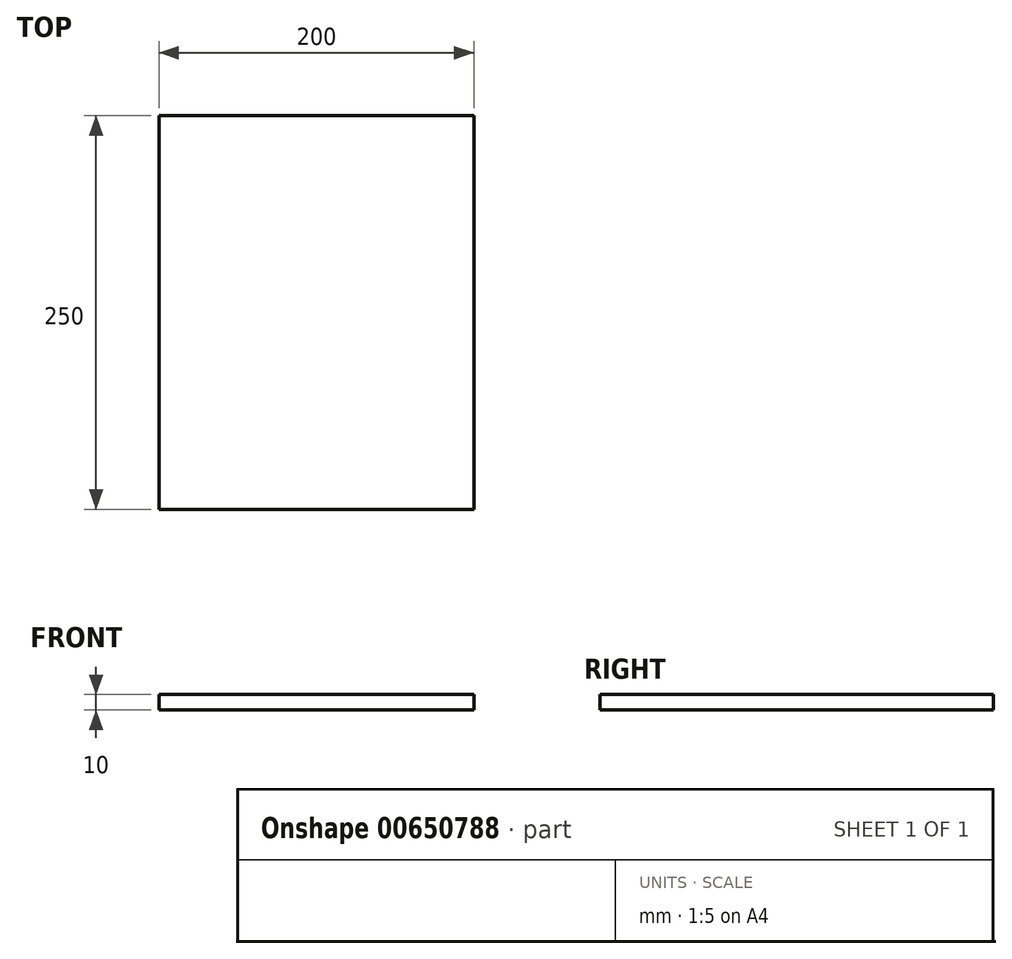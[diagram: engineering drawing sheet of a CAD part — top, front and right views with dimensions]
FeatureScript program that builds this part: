
annotation { "Feature Type Name" : "Feature", "Feature Type Description" : "" }
export const myFeature = defineFeature(function(context is Context, id is Id, definition is map)
    precondition{}
    {
        {
            var Q0;
            Q0=qCreatedBy(makeId("Top.planeOp"),FACE);
            var sketch = newSketch(context, id + "F0", { "sketchPlane" : qUnion([Q0])});
            skLineSegment(sketch, "E0.bottom", {"start": v(-157.02, 200.18) * mm, "end": v(42.98, 200.18) * mm});
            skLineSegment(sketch, "E0.top", {"start": v(-157.02, -49.82) * mm, "end": v(42.98, -49.82) * mm});
            skLineSegment(sketch, "E0.left", {"start": v(-157.02, 200.18) * mm, "end": v(-157.02, -49.82) * mm});
            skLineSegment(sketch, "E0.right", {"start": v(42.98, 200.18) * mm, "end": v(42.98, -49.82) * mm});
            skSolve(sketch);
        }
        {
            var Q0;
            Q0=makeQuery(id+"F0.imprint","IMPRINT",FACE,{"disambiguationData":[TD([[makeQuery(id+"F0.imprint","IMPRINT",EDGE,{"derivedFrom":sQuery(id+"F0.wireOp",EDGE,"E0.bottom")}),-1.0]])]});
            extrude(context, id + "F1", {"entities" : qUnion([Q0]), "depth" : 10 * mm, "offsetDistance" : 25 * mm});
        }
    });
